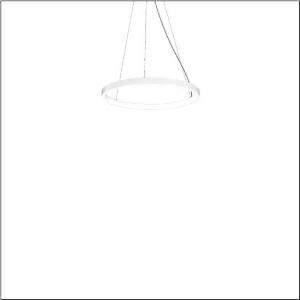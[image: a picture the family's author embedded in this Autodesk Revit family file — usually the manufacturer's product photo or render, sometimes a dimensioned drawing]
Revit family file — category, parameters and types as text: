
# Revit family: silica_21_ring-i_5pjbi1d1004a
name_source: partatom
category: Lighting Fixtures
units: mm (PartAtom-declared; Revit-internal decimal feet)

## family parameters
Cut with Voids When Loaded = No
Host = Face
Light Source = No
Part Type = Normal
Room Calculation Point = No
Round Connector Dimension = Use Diameter
Shared = No

## types (1)
- Silica 21 Ring-I (1 x LED, 3430 lm, 60 W, 3000K)
    Apparent Load = 60 VA
    CIE Flux Codes = 22 48 76 50 101
    Color Rendering = 80
    Color Temperature = 3000K
    Default Elevation = 1800 mm
    Description = Silica 21 Ring-I, suspended luminaire, of PMMA, frosted, light emission: inner ring side luminous distribution, primary light characteristic: symmetric, installation type: suspended mounting, LED, rated luminous flux: 3.430lm, luminous efficacy: 57lm/W, light colour: 830, colour temperature: 3000K, control gear: DALI 2, with terminal, 5-pole, mains connection: 230V, AC/DC, 0/50..60Hz, rated input power: 60W, housing, of extruded aluminium section, traffic white (RAL 9016), diameter: 610mm, ceiling canopy, traffic white (RAL 9016), protection rating (lamp compartment): IP40, insulation class (complete): insulation class I (protective earthing), certification: CE, impact resistance: IK02, permissible operating ambient temperature: 0..+35°C, packaging unit: 1 piece
    Height = 48 mm  [stored 0.15748 ft]
    Lamp = 1 x LED
    Lamp Light Flux = 3430 lm
    Lamp Power = 60 W
    Lamp count = 1
    Length = 610 mm
    Luminous efficacy = 57 lm/W
    Manufacturer = Siteco
    ModVariant = No
    Model = 5PJBI1D1004A
    Mounting Place = Ceiling
    Mounting Type = Pendant
    Number of Poles = 1
    OnlyDefault = Yes
    Power Factor = 1
    Product Name = Silica 21 Ring-I
    Product group = suspended luminaire
    ProductGroupID = 904
    Protection Class = Protection class I
    Protection Degree = IP 40
    RLX_Detail_Level = 1
    RLX_Emergency_Light_Flux = 0 lm
    RLX_Emergency_Type = 0
    RLX_Emergency_Type_DB = No
    RlxData = <blob elided: 10481 chars, md5=0b014170>
    Socket = socket
    Standby Power = 0 W
    System Light Flux = 3430 lm
    System Power = 60 W
    Type Comments = Product without accessories
    Type Image = l_1258363.jpg
    URL = http://relux.com
    VarID = ---
    Voltage = 0 V
    Weight = 0.00 kg
    Width = 0 mm  [stored 0 ft]

note: [stored X ft] marks values corroborated as IEEE doubles in the binary element streams (Revit-internal decimal feet)

## geometry (parser evidence)
native form markers: Sweep x13
no freeform markers — native parametric forms only
